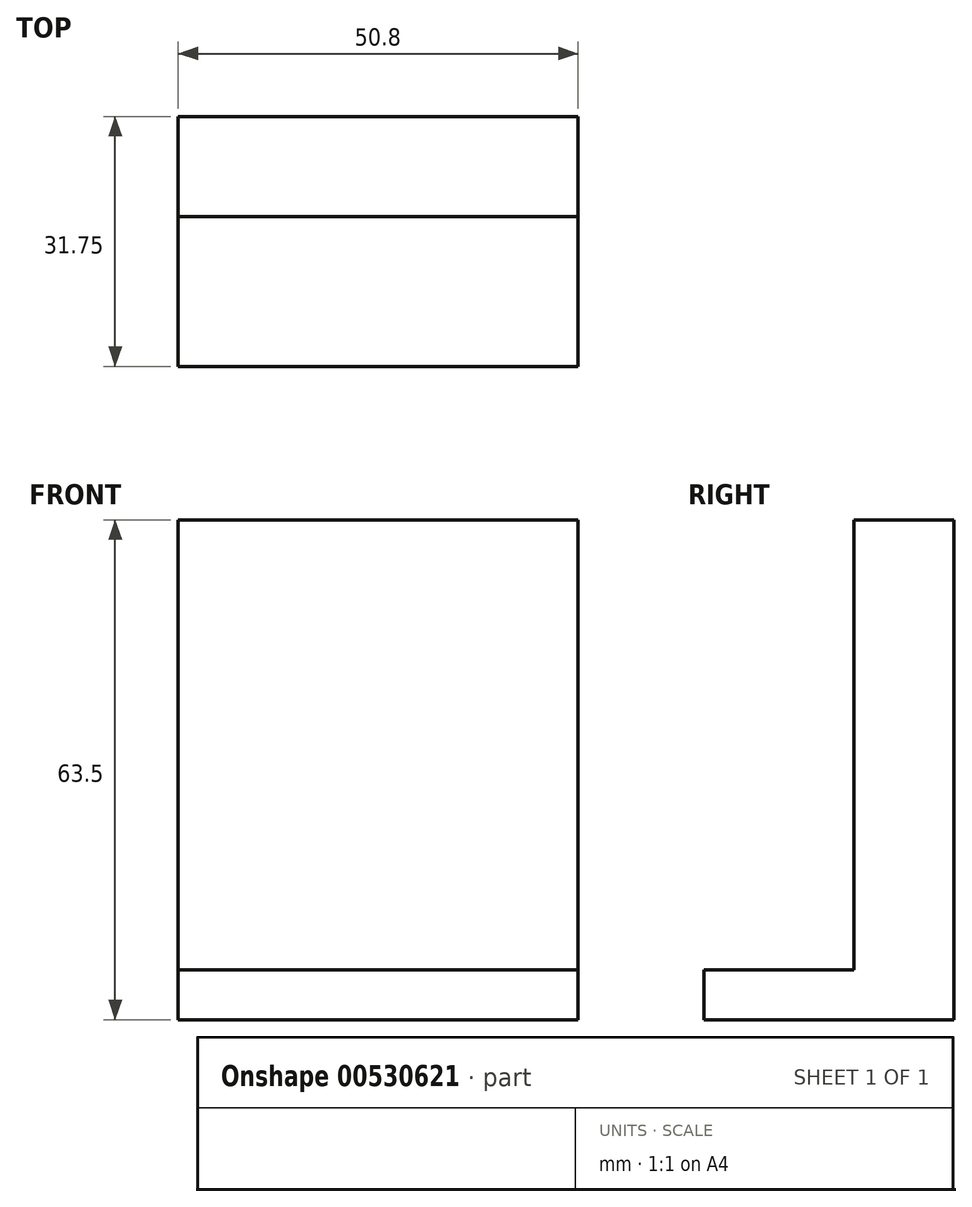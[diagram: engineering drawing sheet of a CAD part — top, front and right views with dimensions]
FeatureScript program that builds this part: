
annotation { "Feature Type Name" : "Feature", "Feature Type Description" : "" }
export const myFeature = defineFeature(function(context is Context, id is Id, definition is map)
    precondition{}
    {
        {
            var Q0;
            Q0=qCreatedBy(makeId("Front.planeOp"),FACE);
            var sketch = newSketch(context, id + "F0", { "sketchPlane" : qUnion([Q0])});
            skLineSegment(sketch, "E0", {"start": v(-67.21, 0) * mm, "end": v(-16.41, 0) * mm});
            skLineSegment(sketch, "E1", {"start": v(-67.21, 0) * mm, "end": v(-67.21, 6.35) * mm});
            skLineSegment(sketch, "E2", {"start": v(-16.41, 0) * mm, "end": v(-16.41, 6.35) * mm});
            skLineSegment(sketch, "E3", {"start": v(-67.21, 6.35) * mm, "end": v(-16.41, 6.35) * mm});
            skSolve(sketch);
        }
        {
            var Q0;
            Q0 = qSketchRegion(id + "F0", true);
            extrude(context, id + "F1", {"entities" : qUnion([Q0]), "depth" : 31.75 * mm, "offsetDistance" : 25.4 * mm});
        }
        {
            var Q0;
            Q0=makeQuery(id+"F1.opExtrude","SWEPT_FACE",FACE,{"disambiguationData":[OSD([sQuery(id+"F0.wireOp",EDGE,"E3")])]});
            var sketch = newSketch(context, id + "F2", { "sketchPlane" : qUnion([Q0])});
            skLineSegment(sketch, "E4", {"start": v(-67.21, -12.7) * mm, "end": v(-16.41, -12.7) * mm});
            skLineSegment(sketch, "E5", {"start": v(-16.41, -12.7) * mm, "end": v(-16.41, 0) * mm});
            skLineSegment(sketch, "E6", {"start": v(-16.41, 0) * mm, "end": v(-67.21, 0) * mm});
            skLineSegment(sketch, "E7", {"start": v(-67.21, 0) * mm, "end": v(-67.21, -12.7) * mm});
            skSolve(sketch);
        }
        {
            var Q0;
            Q0=makeQuery(id+"F2.imprint","IMPRINT",FACE,{"disambiguationData":[TD([[makeQuery(id+"F2.imprint","IMPRINT",EDGE,{"derivedFrom":sQuery(id+"F2.wireOp",EDGE,"E4")}),1.0]])]});
            extrude(context, id + "F3", {"entities" : qUnion([Q0]), "operationType" : NewBodyOperationType.ADD, "depth" : 57.15 * mm, "offsetDistance" : 25.4 * mm});
        }
    });
